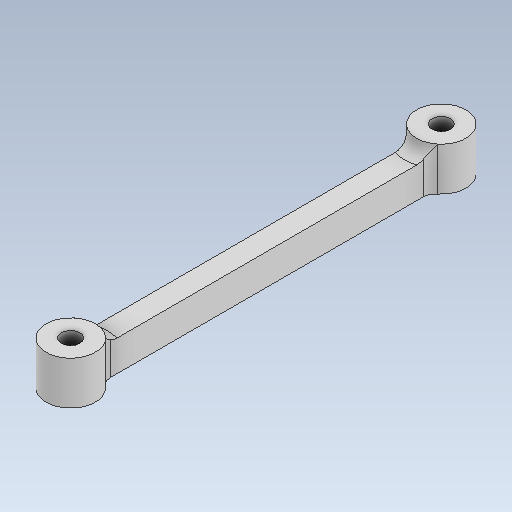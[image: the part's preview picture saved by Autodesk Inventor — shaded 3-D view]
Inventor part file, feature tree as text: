
AUTODESK INVENTOR PART (.ipt)
format: ipt  version: 2020 (Build 240168000, 168)  size: 140,288 bytes
history: native  units: mm
features: sketch x3, projected_geometry x3, extrude x2, hole x1, fillet x1
ambient origin geometry x8: Origin, YZ Plane, XZ Plane, XY Plane, X Axis, Y Axis, Z Axis, Center Point
bodies: Solid1 (feature_tree)
feature tree (10):
  extrude  "Extrusion1"  Depth=60.0mm
  extrude  "Extrusion2"  Depth=3.5mm
  hole  "Hole1"  [1 undecoded]
  fillet  "Fillet1"  Radius=8.0mm
  sketch  "Sketch1"  dims[d0=8.0mm d1=60.0mm]
  sketch  "Sketch2"  dims[d2=8.0mm d3=3.5mm]
  projected_geometry  "Projected Loop1"
  sketch  "Sketch3"  dims[d4=7.0mm d5=0.0mm d6=8.0mm d7=8.0mm d8=2.0mm d9=0.0mm d10=3.0mm d11=6.0mm d12=4.0mm d13=2.0mm d14=90.0deg d15=8.0mm d16=0.0mm d17=2.0mm]
  projected_geometry  "Projected Loop2"
  projected_geometry  "Projected Loop3"
note: 1 required parameter value undecoded (feature->parameter linkage not recoverable at this tier; creation-order binding heuristic only, values carry confidence <= 0.55)
